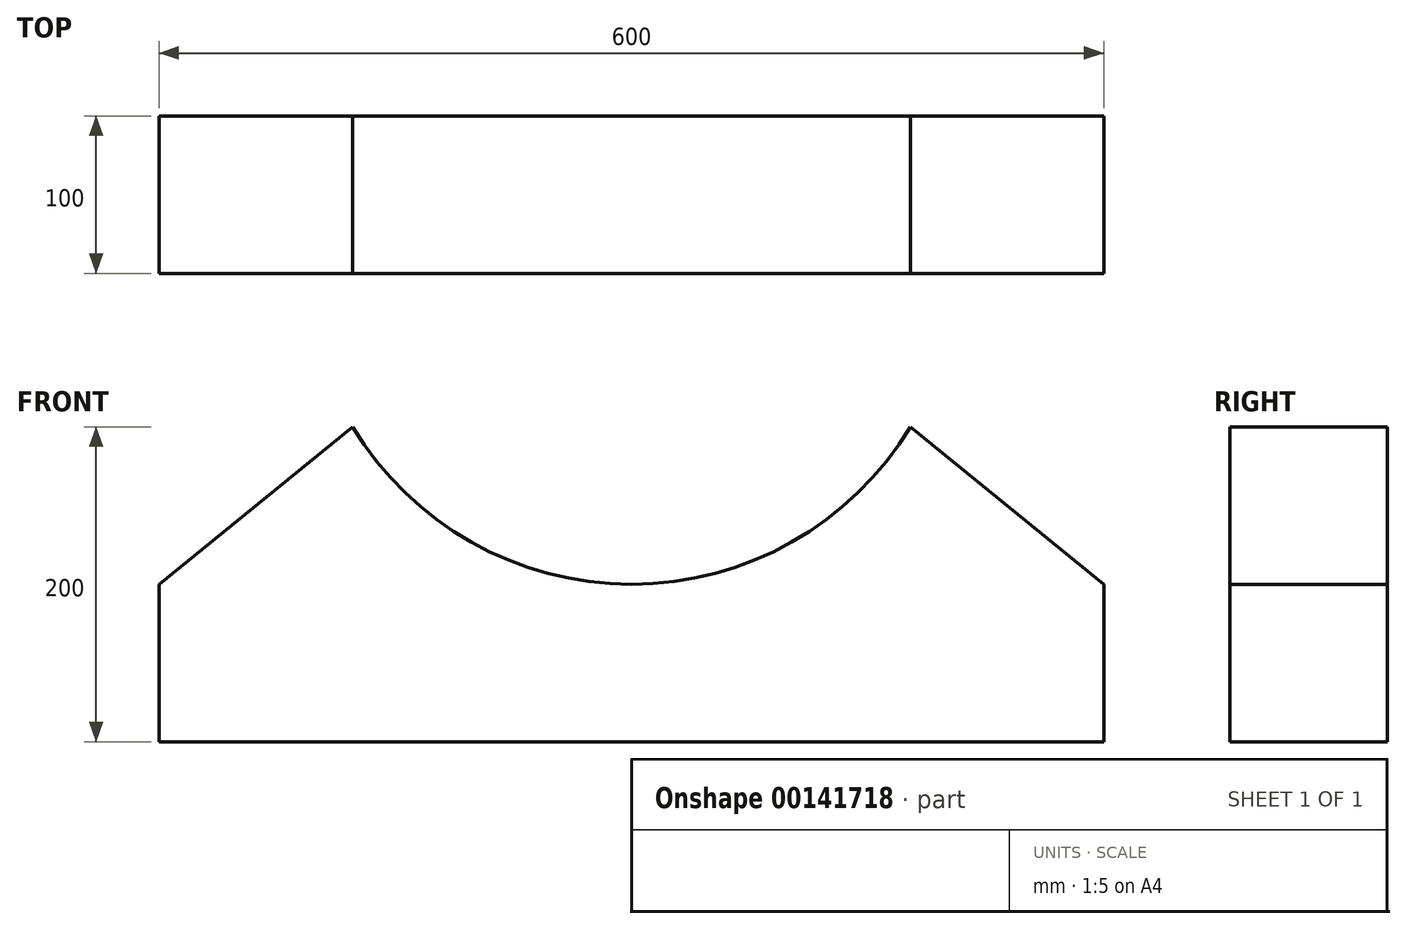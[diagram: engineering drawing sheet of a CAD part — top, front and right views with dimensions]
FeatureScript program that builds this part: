
annotation { "Feature Type Name" : "Feature", "Feature Type Description" : "" }
export const myFeature = defineFeature(function(context is Context, id is Id, definition is map)
    precondition{}
    {
        {
            var Q0;
            Q0=qCreatedBy(makeId("Front.planeOp"),FACE);
            var sketch = newSketch(context, id + "F0", { "sketchPlane" : qUnion([Q0])});
            skLineSegment(sketch, "E0", {"start": v(0, 0) * mm, "end": v(0, 341.45) * mm, "construction": true});
            skLineSegment(sketch, "E1", {"start": v(0, 100) * mm, "end": v(503.59, 100) * mm, "construction": true});
            skLineSegment(sketch, "E2", {"start": v(-300, 0) * mm, "end": v(300, 0) * mm});
            skLineSegment(sketch, "E3", {"start": v(300, 0) * mm, "end": v(300, 100) * mm});
            skLineSegment(sketch, "E4", {"start": v(-300, 0) * mm, "end": v(-300, 100) * mm});
            skLineSegment(sketch, "E5", {"start": v(-300, 100) * mm, "end": v(-177.2, 200) * mm});
            skLineSegment(sketch, "E6", {"start": v(300, 100) * mm, "end": v(177.2, 200) * mm});
            skArc(sketch, "E7", {"start": v(-177.2, 200) * mm, "mid": v(0, 100) * mm, "end": v(177.2, 200) * mm});
            skSolve(sketch);
        }
        {
            var Q0;
            Q0=makeQuery(id+"F0.imprint","IMPRINT",FACE,{"disambiguationData":[TD([[makeQuery(id+"F0.imprint","IMPRINT",EDGE,{"derivedFrom":sQuery(id+"F0.wireOp",EDGE,"E2")}),1.0]])]});
            extrude(context, id + "F1", {"entities" : qUnion([Q0]), "depth" : 100 * mm});
        }
    });
